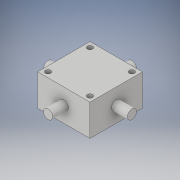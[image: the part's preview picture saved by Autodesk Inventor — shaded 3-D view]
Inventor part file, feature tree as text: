
AUTODESK INVENTOR PART (.ipt)
format: ipt  version: 2018 (Build 220112000, 112)  size: 136,192 bytes
history: native  units: in
note: dims shown in document units (in); Inventor stores cm internally (conversion verified against a paired STEP export)
features: extrude x6, sketch x6
ambient origin geometry x8: Origin, YZ Plane, XZ Plane, XY Plane, X Axis, Y Axis, Z Axis, Center Point
bodies: Solid1 (feature_tree)
feature tree (12):
  extrude  "Extrusion1"  Depth=1.25in
  extrude  "Extrusion2"  Depth=0.75in
  sketch  "Sketch3"  dims[d5=0.125in d6=0.125in]
  sketch  "Sketch4"  dims[d7=0.125in d8=0.0in d9=0.0in]
  sketch  "Sketch5"  dims[d10=0.22in d11=0.22in]
  extrude  "Extrusion3"  Depth=0.125in
  extrude  "Extrusion4"  TaperAngle=0.0deg  [1 undecoded]
  extrude  "Extrusion5"  Depth=0.22in
  extrude  "Extrusion6"  Depth=0.375in
  sketch  "Sketch1"  dims[d0=1.25in d1=1.25in]
  sketch  "Sketch2"  dims[d2=0.75in d3=0.0in d4=0.125in]
  sketch  "Sketch6"  dims[d12=0.22in d13=0.22in d14=0.375in d15=0.0in d16=0.375in d17=0.0in d18=0.375in d19=0.0in d20=0.375in d21=0.0in]
note: 1 required parameter value undecoded (feature->parameter linkage not recoverable at this tier; creation-order binding heuristic only, values carry confidence <= 0.55)
